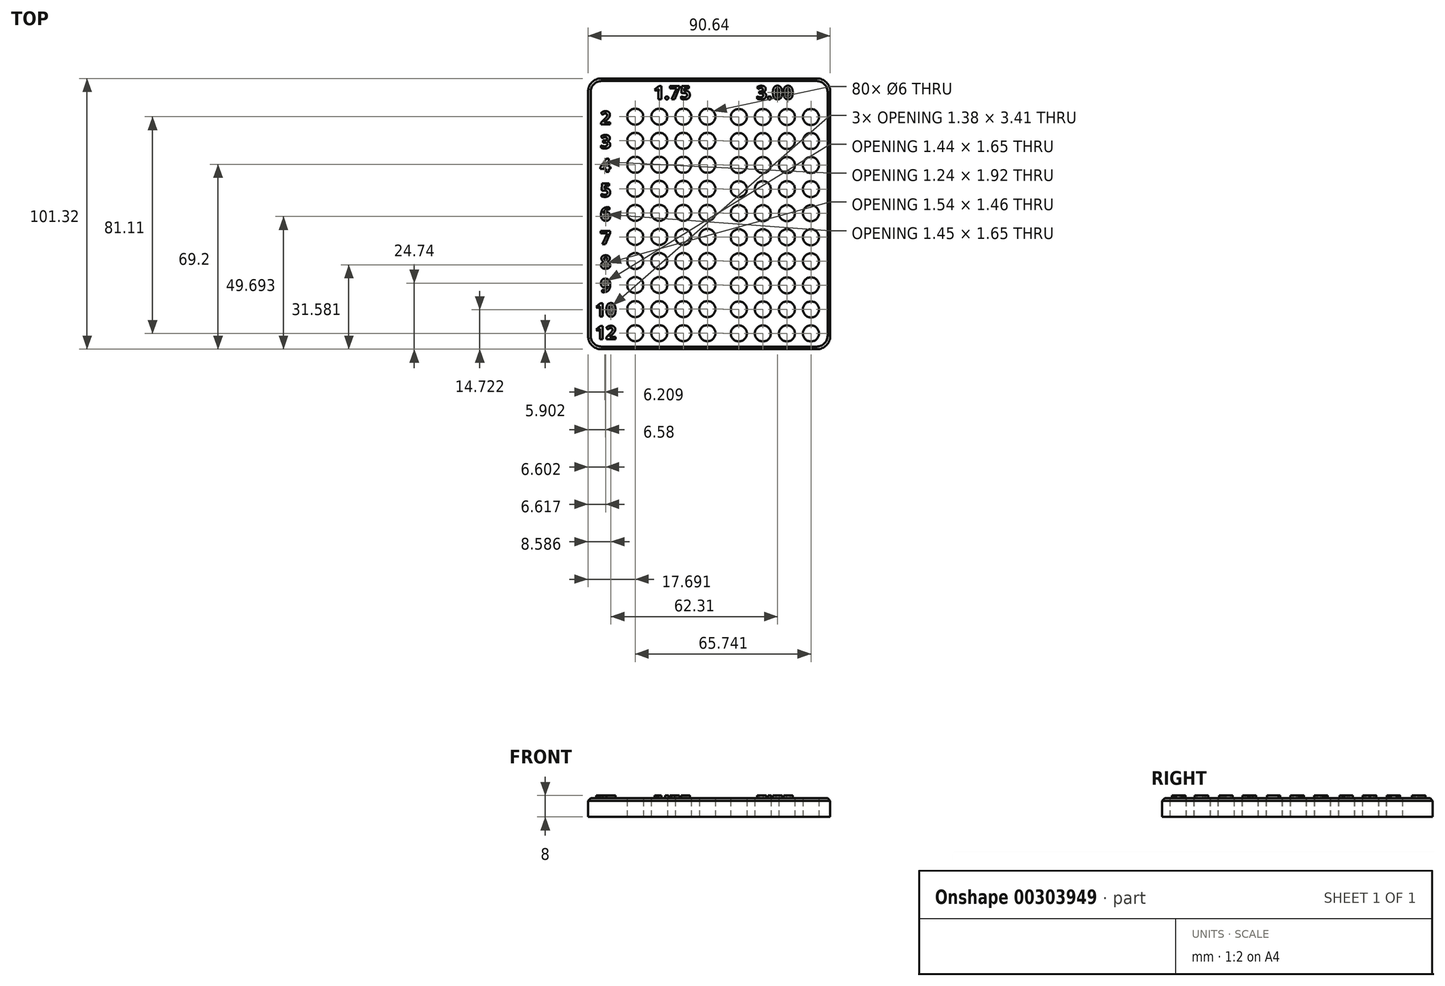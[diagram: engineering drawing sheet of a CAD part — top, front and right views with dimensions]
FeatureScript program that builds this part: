
annotation { "Feature Type Name" : "Feature", "Feature Type Description" : "" }
export const myFeature = defineFeature(function(context is Context, id is Id, definition is map)
    precondition{}
    {
        {
            var Q0;
            Q0=qCreatedBy(makeId("Top.planeOp"),FACE);
            var sketch = newSketch(context, id + "F0", { "sketchPlane" : qUnion([Q0])});
            skPoint(sketch, "E0.middle", {"position": v(0, 0) * mm});
            skCircle(sketch, "E1", {"center": v(-28.9, 13.21) * mm, "radius": 3 * mm});
            skCircle(sketch, "E2.0.1.0", {"center": v(-28.9, 4.21) * mm, "radius": 3 * mm});
            skCircle(sketch, "E2.0.2.0", {"center": v(-28.9, -4.79) * mm, "radius": 3 * mm});
            skCircle(sketch, "E2.0.3.0", {"center": v(-28.9, -13.79) * mm, "radius": 3 * mm});
            skCircle(sketch, "E2.0.4.0", {"center": v(-28.9, -22.79) * mm, "radius": 3 * mm});
            skCircle(sketch, "E2.0.5.0", {"center": v(-28.9, -31.79) * mm, "radius": 3 * mm});
            skCircle(sketch, "E2.0.6.0", {"center": v(-28.9, -40.79) * mm, "radius": 3 * mm});
            skCircle(sketch, "E2.0.7.0", {"center": v(-28.9, -49.79) * mm, "radius": 3 * mm});
            skCircle(sketch, "E2.0.8.0", {"center": v(-28.9, -58.79) * mm, "radius": 3 * mm});
            skCircle(sketch, "E2.0.9.0", {"center": v(-28.9, -67.79) * mm, "radius": 3 * mm});
            skCircle(sketch, "E2.1.0.0", {"center": v(-19.9, 13.21) * mm, "radius": 3 * mm});
            skCircle(sketch, "E2.1.1.0", {"center": v(-19.9, 4.21) * mm, "radius": 3 * mm});
            skCircle(sketch, "E2.1.2.0", {"center": v(-19.9, -4.79) * mm, "radius": 3 * mm});
            skCircle(sketch, "E2.1.3.0", {"center": v(-19.9, -13.79) * mm, "radius": 3 * mm});
            skCircle(sketch, "E2.1.4.0", {"center": v(-19.9, -22.79) * mm, "radius": 3 * mm});
            skCircle(sketch, "E2.1.5.0", {"center": v(-19.9, -31.79) * mm, "radius": 3 * mm});
            skCircle(sketch, "E2.1.6.0", {"center": v(-19.9, -40.79) * mm, "radius": 3 * mm});
            skCircle(sketch, "E2.1.7.0", {"center": v(-19.9, -49.79) * mm, "radius": 3 * mm});
            skCircle(sketch, "E2.1.8.0", {"center": v(-19.9, -58.79) * mm, "radius": 3 * mm});
            skCircle(sketch, "E2.1.9.0", {"center": v(-19.9, -67.79) * mm, "radius": 3 * mm});
            skCircle(sketch, "E2.2.0.0", {"center": v(-10.9, 13.21) * mm, "radius": 3 * mm});
            skCircle(sketch, "E2.2.1.0", {"center": v(-10.9, 4.21) * mm, "radius": 3 * mm});
            skCircle(sketch, "E2.2.2.0", {"center": v(-10.9, -4.79) * mm, "radius": 3 * mm});
            skCircle(sketch, "E2.2.3.0", {"center": v(-10.9, -13.79) * mm, "radius": 3 * mm});
            skCircle(sketch, "E2.2.4.0", {"center": v(-10.9, -22.79) * mm, "radius": 3 * mm});
            skCircle(sketch, "E2.2.5.0", {"center": v(-10.9, -31.79) * mm, "radius": 3 * mm});
            skCircle(sketch, "E2.2.6.0", {"center": v(-10.9, -40.79) * mm, "radius": 3 * mm});
            skCircle(sketch, "E2.2.7.0", {"center": v(-10.9, -49.79) * mm, "radius": 3 * mm});
            skCircle(sketch, "E2.2.8.0", {"center": v(-10.9, -58.79) * mm, "radius": 3 * mm});
            skCircle(sketch, "E2.2.9.0", {"center": v(-10.9, -67.79) * mm, "radius": 3 * mm});
            skCircle(sketch, "E2.3.0.0", {"center": v(-1.9, 13.21) * mm, "radius": 3 * mm});
            skCircle(sketch, "E2.3.1.0", {"center": v(-1.9, 4.21) * mm, "radius": 3 * mm});
            skCircle(sketch, "E2.3.2.0", {"center": v(-1.9, -4.79) * mm, "radius": 3 * mm});
            skCircle(sketch, "E2.3.3.0", {"center": v(-1.9, -13.79) * mm, "radius": 3 * mm});
            skCircle(sketch, "E2.3.4.0", {"center": v(-1.9, -22.79) * mm, "radius": 3 * mm});
            skCircle(sketch, "E2.3.5.0", {"center": v(-1.9, -31.79) * mm, "radius": 3 * mm});
            skCircle(sketch, "E2.3.6.0", {"center": v(-1.9, -40.79) * mm, "radius": 3 * mm});
            skCircle(sketch, "E2.3.7.0", {"center": v(-1.9, -49.79) * mm, "radius": 3 * mm});
            skCircle(sketch, "E2.3.8.0", {"center": v(-1.9, -58.79) * mm, "radius": 3 * mm});
            skCircle(sketch, "E2.3.9.0", {"center": v(-1.9, -67.79) * mm, "radius": 3 * mm});
            skLineSegment(sketch, "E2.direction1", {"start": v(-28.9, 13.21) * mm, "end": v(-19.9, 13.21) * mm, "construction": true});
            skLineSegment(sketch, "E2.direction2", {"start": v(-28.9, 13.21) * mm, "end": v(-28.9, 4.21) * mm, "construction": true});
            skPoint(sketch, "E3.middle", {"position": v(104.25, 33.67) * mm});
            skCircle(sketch, "E4", {"center": v(9.84, 13.1) * mm, "radius": 3 * mm});
            skCircle(sketch, "E5.0.1.0", {"center": v(9.84, 4.1) * mm, "radius": 3 * mm});
            skCircle(sketch, "E5.0.2.0", {"center": v(9.84, -4.9) * mm, "radius": 3 * mm});
            skCircle(sketch, "E5.0.3.0", {"center": v(9.84, -13.9) * mm, "radius": 3 * mm});
            skCircle(sketch, "E5.0.4.0", {"center": v(9.84, -22.9) * mm, "radius": 3 * mm});
            skCircle(sketch, "E5.0.5.0", {"center": v(9.84, -31.9) * mm, "radius": 3 * mm});
            skCircle(sketch, "E5.0.6.0", {"center": v(9.84, -40.9) * mm, "radius": 3 * mm});
            skCircle(sketch, "E5.0.7.0", {"center": v(9.84, -49.9) * mm, "radius": 3 * mm});
            skCircle(sketch, "E5.0.8.0", {"center": v(9.84, -58.9) * mm, "radius": 3 * mm});
            skCircle(sketch, "E5.0.9.0", {"center": v(9.84, -67.9) * mm, "radius": 3 * mm});
            skCircle(sketch, "E5.1.0.0", {"center": v(18.84, 13.1) * mm, "radius": 3 * mm});
            skCircle(sketch, "E5.1.1.0", {"center": v(18.84, 4.1) * mm, "radius": 3 * mm});
            skCircle(sketch, "E5.1.2.0", {"center": v(18.84, -4.9) * mm, "radius": 3 * mm});
            skCircle(sketch, "E5.1.3.0", {"center": v(18.84, -13.9) * mm, "radius": 3 * mm});
            skCircle(sketch, "E5.1.4.0", {"center": v(18.84, -22.9) * mm, "radius": 3 * mm});
            skCircle(sketch, "E5.1.5.0", {"center": v(18.84, -31.9) * mm, "radius": 3 * mm});
            skCircle(sketch, "E5.1.6.0", {"center": v(18.84, -40.9) * mm, "radius": 3 * mm});
            skCircle(sketch, "E5.1.7.0", {"center": v(18.84, -49.9) * mm, "radius": 3 * mm});
            skCircle(sketch, "E5.1.8.0", {"center": v(18.84, -58.9) * mm, "radius": 3 * mm});
            skCircle(sketch, "E5.1.9.0", {"center": v(18.84, -67.9) * mm, "radius": 3 * mm});
            skCircle(sketch, "E5.2.0.0", {"center": v(27.84, 13.1) * mm, "radius": 3 * mm});
            skCircle(sketch, "E5.2.1.0", {"center": v(27.84, 4.1) * mm, "radius": 3 * mm});
            skCircle(sketch, "E5.2.2.0", {"center": v(27.84, -4.9) * mm, "radius": 3 * mm});
            skCircle(sketch, "E5.2.3.0", {"center": v(27.84, -13.9) * mm, "radius": 3 * mm});
            skCircle(sketch, "E5.2.4.0", {"center": v(27.84, -22.9) * mm, "radius": 3 * mm});
            skCircle(sketch, "E5.2.5.0", {"center": v(27.84, -31.9) * mm, "radius": 3 * mm});
            skCircle(sketch, "E5.2.6.0", {"center": v(27.84, -40.9) * mm, "radius": 3 * mm});
            skCircle(sketch, "E5.2.7.0", {"center": v(27.84, -49.9) * mm, "radius": 3 * mm});
            skCircle(sketch, "E5.2.8.0", {"center": v(27.84, -58.9) * mm, "radius": 3 * mm});
            skCircle(sketch, "E5.2.9.0", {"center": v(27.84, -67.9) * mm, "radius": 3 * mm});
            skCircle(sketch, "E5.3.0.0", {"center": v(36.84, 13.1) * mm, "radius": 3 * mm});
            skCircle(sketch, "E5.3.1.0", {"center": v(36.84, 4.1) * mm, "radius": 3 * mm});
            skCircle(sketch, "E5.3.2.0", {"center": v(36.84, -4.9) * mm, "radius": 3 * mm});
            skCircle(sketch, "E5.3.3.0", {"center": v(36.84, -13.9) * mm, "radius": 3 * mm});
            skCircle(sketch, "E5.3.4.0", {"center": v(36.84, -22.9) * mm, "radius": 3 * mm});
            skCircle(sketch, "E5.3.5.0", {"center": v(36.84, -31.9) * mm, "radius": 3 * mm});
            skCircle(sketch, "E5.3.6.0", {"center": v(36.84, -40.9) * mm, "radius": 3 * mm});
            skCircle(sketch, "E5.3.7.0", {"center": v(36.84, -49.9) * mm, "radius": 3 * mm});
            skCircle(sketch, "E5.3.8.0", {"center": v(36.84, -58.9) * mm, "radius": 3 * mm});
            skCircle(sketch, "E5.3.9.0", {"center": v(36.84, -67.9) * mm, "radius": 3 * mm});
            skLineSegment(sketch, "E5.direction1", {"start": v(9.84, 13.1) * mm, "end": v(18.84, 13.1) * mm, "construction": true});
            skLineSegment(sketch, "E5.direction2", {"start": v(9.84, 13.1) * mm, "end": v(9.84, 4.1) * mm, "construction": true});
            skLineSegment(sketch, "E6.bottom", {"start": v(-46.59, 27.52) * mm, "end": v(44.05, 27.52) * mm});
            skLineSegment(sketch, "E6.top", {"start": v(-46.59, -73.8) * mm, "end": v(44.05, -73.8) * mm});
            skLineSegment(sketch, "E6.left", {"start": v(-46.59, 27.52) * mm, "end": v(-46.59, -73.8) * mm});
            skLineSegment(sketch, "E6.right", {"start": v(44.05, 27.52) * mm, "end": v(44.05, -73.8) * mm});
            skSolve(sketch);
        }
        {
            var Q0;
            Q0 = qSketchRegion(id + "F0", true);
            extrude(context, id + "F1", {"entities" : qUnion([Q0]), "depth" : 7 * mm});
        }
        {
            var Q0;
            Q0=makeQuery(id+"F1.opExtrude","CAP_FACE",FACE,{"disambiguationData":[OSD([sQuery(id+"F0.wireOp",EDGE,"E1"),sQuery(id+"F0.wireOp",EDGE,"E2.0.1.0"),sQuery(id+"F0.wireOp",EDGE,"E2.0.2.0"),sQuery(id+"F0.wireOp",EDGE,"E2.0.3.0"),sQuery(id+"F0.wireOp",EDGE,"E2.0.4.0"),sQuery(id+"F0.wireOp",EDGE,"E2.0.5.0"),sQuery(id+"F0.wireOp",EDGE,"E2.0.6.0"),sQuery(id+"F0.wireOp",EDGE,"E2.0.7.0"),sQuery(id+"F0.wireOp",EDGE,"E2.0.8.0"),sQuery(id+"F0.wireOp",EDGE,"E2.0.9.0"),sQuery(id+"F0.wireOp",EDGE,"E2.1.0.0"),sQuery(id+"F0.wireOp",EDGE,"E2.1.1.0"),sQuery(id+"F0.wireOp",EDGE,"E2.1.2.0"),sQuery(id+"F0.wireOp",EDGE,"E2.1.3.0"),sQuery(id+"F0.wireOp",EDGE,"E2.1.4.0"),sQuery(id+"F0.wireOp",EDGE,"E2.1.5.0"),sQuery(id+"F0.wireOp",EDGE,"E2.1.6.0"),sQuery(id+"F0.wireOp",EDGE,"E2.1.7.0"),sQuery(id+"F0.wireOp",EDGE,"E2.1.8.0"),sQuery(id+"F0.wireOp",EDGE,"E2.1.9.0"),sQuery(id+"F0.wireOp",EDGE,"E2.2.0.0"),sQuery(id+"F0.wireOp",EDGE,"E2.2.1.0"),sQuery(id+"F0.wireOp",EDGE,"E2.2.2.0"),sQuery(id+"F0.wireOp",EDGE,"E2.2.3.0"),sQuery(id+"F0.wireOp",EDGE,"E2.2.4.0"),sQuery(id+"F0.wireOp",EDGE,"E2.2.5.0"),sQuery(id+"F0.wireOp",EDGE,"E2.2.6.0"),sQuery(id+"F0.wireOp",EDGE,"E2.2.7.0"),sQuery(id+"F0.wireOp",EDGE,"E2.2.8.0"),sQuery(id+"F0.wireOp",EDGE,"E2.2.9.0"),sQuery(id+"F0.wireOp",EDGE,"E2.3.0.0"),sQuery(id+"F0.wireOp",EDGE,"E2.3.1.0"),sQuery(id+"F0.wireOp",EDGE,"E2.3.2.0"),sQuery(id+"F0.wireOp",EDGE,"E2.3.3.0"),sQuery(id+"F0.wireOp",EDGE,"E2.3.4.0"),sQuery(id+"F0.wireOp",EDGE,"E2.3.5.0"),sQuery(id+"F0.wireOp",EDGE,"E2.3.6.0"),sQuery(id+"F0.wireOp",EDGE,"E2.3.7.0"),sQuery(id+"F0.wireOp",EDGE,"E2.3.8.0"),sQuery(id+"F0.wireOp",EDGE,"E2.3.9.0"),sQuery(id+"F0.wireOp",EDGE,"E4"),sQuery(id+"F0.wireOp",EDGE,"E5.0.1.0"),sQuery(id+"F0.wireOp",EDGE,"E5.0.2.0"),sQuery(id+"F0.wireOp",EDGE,"E5.0.3.0"),sQuery(id+"F0.wireOp",EDGE,"E5.0.4.0"),sQuery(id+"F0.wireOp",EDGE,"E5.0.5.0"),sQuery(id+"F0.wireOp",EDGE,"E5.0.6.0"),sQuery(id+"F0.wireOp",EDGE,"E5.0.7.0"),sQuery(id+"F0.wireOp",EDGE,"E5.0.8.0"),sQuery(id+"F0.wireOp",EDGE,"E5.0.9.0"),sQuery(id+"F0.wireOp",EDGE,"E5.1.0.0"),sQuery(id+"F0.wireOp",EDGE,"E5.1.1.0"),sQuery(id+"F0.wireOp",EDGE,"E5.1.2.0"),sQuery(id+"F0.wireOp",EDGE,"E5.1.3.0"),sQuery(id+"F0.wireOp",EDGE,"E5.1.4.0"),sQuery(id+"F0.wireOp",EDGE,"E5.1.5.0"),sQuery(id+"F0.wireOp",EDGE,"E5.1.6.0"),sQuery(id+"F0.wireOp",EDGE,"E5.1.7.0"),sQuery(id+"F0.wireOp",EDGE,"E5.1.8.0"),sQuery(id+"F0.wireOp",EDGE,"E5.1.9.0"),sQuery(id+"F0.wireOp",EDGE,"E5.2.0.0"),sQuery(id+"F0.wireOp",EDGE,"E5.2.1.0"),sQuery(id+"F0.wireOp",EDGE,"E5.2.2.0"),sQuery(id+"F0.wireOp",EDGE,"E5.2.3.0"),sQuery(id+"F0.wireOp",EDGE,"E5.2.4.0"),sQuery(id+"F0.wireOp",EDGE,"E5.2.5.0"),sQuery(id+"F0.wireOp",EDGE,"E5.2.6.0"),sQuery(id+"F0.wireOp",EDGE,"E5.2.7.0"),sQuery(id+"F0.wireOp",EDGE,"E5.2.8.0"),sQuery(id+"F0.wireOp",EDGE,"E5.2.9.0"),sQuery(id+"F0.wireOp",EDGE,"E5.3.0.0"),sQuery(id+"F0.wireOp",EDGE,"E5.3.1.0"),sQuery(id+"F0.wireOp",EDGE,"E5.3.2.0"),sQuery(id+"F0.wireOp",EDGE,"E5.3.3.0"),sQuery(id+"F0.wireOp",EDGE,"E5.3.4.0"),sQuery(id+"F0.wireOp",EDGE,"E5.3.5.0"),sQuery(id+"F0.wireOp",EDGE,"E5.3.6.0"),sQuery(id+"F0.wireOp",EDGE,"E5.3.7.0"),sQuery(id+"F0.wireOp",EDGE,"E5.3.8.0"),sQuery(id+"F0.wireOp",EDGE,"E5.3.9.0"),sQuery(id+"F0.wireOp",EDGE,"E6.bottom"),sQuery(id+"F0.wireOp",EDGE,"E6.top"),sQuery(id+"F0.wireOp",EDGE,"E6.left"),sQuery(id+"F0.wireOp",EDGE,"E6.right")])],"isStart":false});
            var sketch = newSketch(context, id + "F2", { "sketchPlane" : qUnion([Q0])});
            skText(sketch, "E7", { "text": "1.75", "fontName": "OpenSans-Bold.ttf"});
            skText(sketch, "E8", { "text": "3.00", "fontName": "OpenSans-Bold.ttf"});
            skText(sketch, "E9", { "text": "2", "fontName": "OpenSans-Bold.ttf"});
            skText(sketch, "E10", { "text": "3", "fontName": "OpenSans-Bold.ttf"});
            skText(sketch, "E11", { "text": "4", "fontName": "OpenSans-Bold.ttf"});
            skText(sketch, "E12", { "text": "5", "fontName": "OpenSans-Bold.ttf"});
            skText(sketch, "E13", { "text": "6", "fontName": "OpenSans-Bold.ttf"});
            skText(sketch, "E14", { "text": "7", "fontName": "OpenSans-Bold.ttf"});
            skText(sketch, "E15", { "text": "8", "fontName": "OpenSans-Bold.ttf"});
            skText(sketch, "E16", { "text": "9", "fontName": "OpenSans-Bold.ttf"});
            skText(sketch, "E17", { "text": "10", "fontName": "OpenSans-Bold.ttf"});
            skText(sketch, "E18", { "text": "12", "fontName": "OpenSans-Bold.ttf"});
            const initialGuessF2  = {"E7": [-0.02203, 0.01974, 1, 0, 0.005], "E8": [0.01638, 0.01974, 1, 0, 0.005], "E9": [-0.04198, 0.01027, 1, 0, 0.005], "E10": [-0.04196, 0.00136, 1, 0, 0.005], "E11": [-0.04204, -0.0074, 1, 0, 0.005], "E12": [-0.04193, -0.01675, 1, 0, 0.005], "E13": [-0.04198, -0.0257, 1, 0, 0.005], "E14": [-0.04198, -0.03455, 1, 0, 0.005], "E15": [-0.04197, -0.04365, 1, 0, 0.005], "E16": [-0.04197, -0.05241, 1, 0, 0.005], "E17": [-0.04395, -0.06156, 1, 0, 0.005], "E18": [-0.04396, -0.07003, 1, 0, 0.005]};
            skSetInitialGuess(sketch, initialGuessF2);
            skSolve(sketch);
        }
        {
            var Q0;
            Q0 = qSketchRegion(id + "F2", true);
            extrude(context, id + "F3", {"entities" : qUnion([Q0]), "depth" : 1 * mm});
        }
        {
            var Q0;
            Q0=makeQuery(id+"F1.opExtrude","SWEPT_EDGE",EDGE,{"disambiguationData":[OSD([sQuery(id+"F0.wireOp",EDGE,"E6.top"),sQuery(id+"F0.wireOp",EDGE,"E6.left")])]});
            var Q1;
            Q1=makeQuery(id+"F1.opExtrude","SWEPT_EDGE",EDGE,{"disambiguationData":[OSD([sQuery(id+"F0.wireOp",EDGE,"E6.top"),sQuery(id+"F0.wireOp",EDGE,"E6.right")])]});
            var Q2;
            Q2=makeQuery(id+"F1.opExtrude","SWEPT_EDGE",EDGE,{"disambiguationData":[OSD([sQuery(id+"F0.wireOp",EDGE,"E6.bottom"),sQuery(id+"F0.wireOp",EDGE,"E6.right")])]});
            var Q3;
            Q3=makeQuery(id+"F1.opExtrude","SWEPT_EDGE",EDGE,{"disambiguationData":[OSD([sQuery(id+"F0.wireOp",EDGE,"E6.bottom"),sQuery(id+"F0.wireOp",EDGE,"E6.left")])]});
            fillet(context, id + "F4", {"entities" : qUnion([Q0, Q1, Q2, Q3]), "radius" : 5 * mm, "tangentPropagation" : true, "allowEdgeOverflow" : false});
        }
        {
            var Q0;
            Q0=makeQuery(id+"F1.opExtrude","CAP_EDGE",EDGE,{"disambiguationData":[OSD([sQuery(id+"F0.wireOp",EDGE,"E6.bottom")])],"isStart":false});
            chamfer(context, id + "F5", {"entities" : qUnion([Q0]), "width" : 1 * mm, "tangentPropagation" : true});
        }
    });
